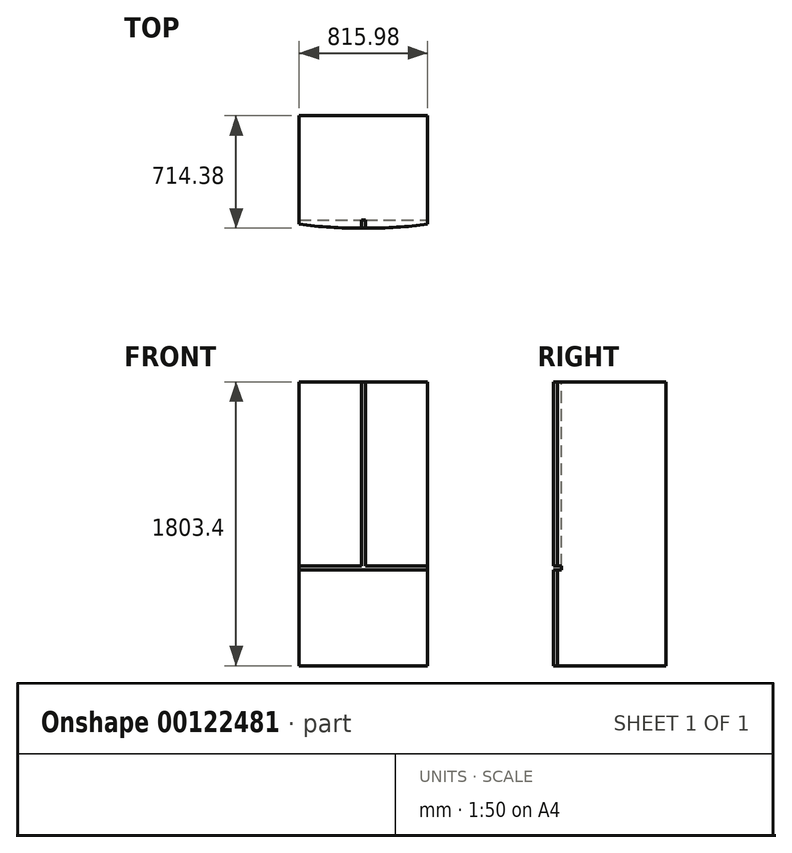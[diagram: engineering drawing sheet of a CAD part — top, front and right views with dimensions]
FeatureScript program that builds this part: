
annotation { "Feature Type Name" : "Feature", "Feature Type Description" : "" }
export const myFeature = defineFeature(function(context is Context, id is Id, definition is map)
    precondition{}
    {
        {
            var Q0;
            Q0=qCreatedBy(makeId("Top.planeOp"),FACE);
            var sketch = newSketch(context, id + "F0", { "sketchPlane" : qUnion([Q0])});
            skLineSegment(sketch, "E0", {"start": v(-407.99, 714.38) * mm, "end": v(407.99, 714.38) * mm});
            skLineSegment(sketch, "E1", {"start": v(407.99, 714.38) * mm, "end": v(407.99, 25.4) * mm});
            skLineSegment(sketch, "E2", {"start": v(-407.99, 25.4) * mm, "end": v(-407.99, 714.37) * mm});
            skArc(sketch, "E3", {"start": v(-407.99, 25.4) * mm, "mid": v(0, 0) * mm, "end": v(407.99, 25.4) * mm});
            skLineSegment(sketch, "E4", {"start": v(-407.99, 25.4) * mm, "end": v(407.99, 25.4) * mm, "construction": true});
            skSolve(sketch);
        }
        {
            var Q0;
            Q0 = qSketchRegion(id + "F0", true);
            extrude(context, id + "F1", {"entities" : qUnion([Q0]), "depth" : 1803.4 * mm});
        }
        {
            var Q0;
            Q0=qCreatedBy(makeId("Front.planeOp"),FACE);
            var sketch = newSketch(context, id + "F2", { "sketchPlane" : qUnion([Q0])});
            skLineSegment(sketch, "E5.bottom", {"start": v(-635, 609.6) * mm, "end": v(635, 609.6) * mm});
            skLineSegment(sketch, "E5.top", {"start": v(-635, 635) * mm, "end": v(635, 635) * mm});
            skLineSegment(sketch, "E5.left", {"start": v(-635, 609.6) * mm, "end": v(-635, 635) * mm});
            skLineSegment(sketch, "E5.right", {"start": v(635, 609.6) * mm, "end": v(635, 635) * mm});
            skLineSegment(sketch, "E6", {"start": v(0, 609.6) * mm, "end": v(0, 0) * mm});
            skSolve(sketch);
        }
        {
            var Q0;
            Q0=qCreatedBy(makeId("Front.planeOp"),FACE);
            var sketch = newSketch(context, id + "F3", { "sketchPlane" : qUnion([Q0])});
            skLineSegment(sketch, "E7.bottom", {"start": v(-12.7, 609.6) * mm, "end": v(12.7, 609.6) * mm});
            skLineSegment(sketch, "E7.top", {"start": v(-12.7, 3149.6) * mm, "end": v(12.7, 3149.6) * mm});
            skLineSegment(sketch, "E7.left", {"start": v(-12.7, 609.6) * mm, "end": v(-12.7, 3149.6) * mm});
            skLineSegment(sketch, "E7.right", {"start": v(12.7, 609.6) * mm, "end": v(12.7, 3149.6) * mm});
            skSolve(sketch);
        }
        {
            var Q0;
            Q0 = qSketchRegion(id + "F2", true);
            extrude(context, id + "F4", {"entities" : qUnion([Q0]), "operationType" : NewBodyOperationType.REMOVE, "oppositeDirection" : true, "depth" : 50.8 * mm});
        }
        {
            var Q0;
            Q0 = qSketchRegion(id + "F3", true);
            extrude(context, id + "F5", {"entities" : qUnion([Q0]), "operationType" : NewBodyOperationType.REMOVE, "oppositeDirection" : true, "depth" : 50.8 * mm});
        }
    });
